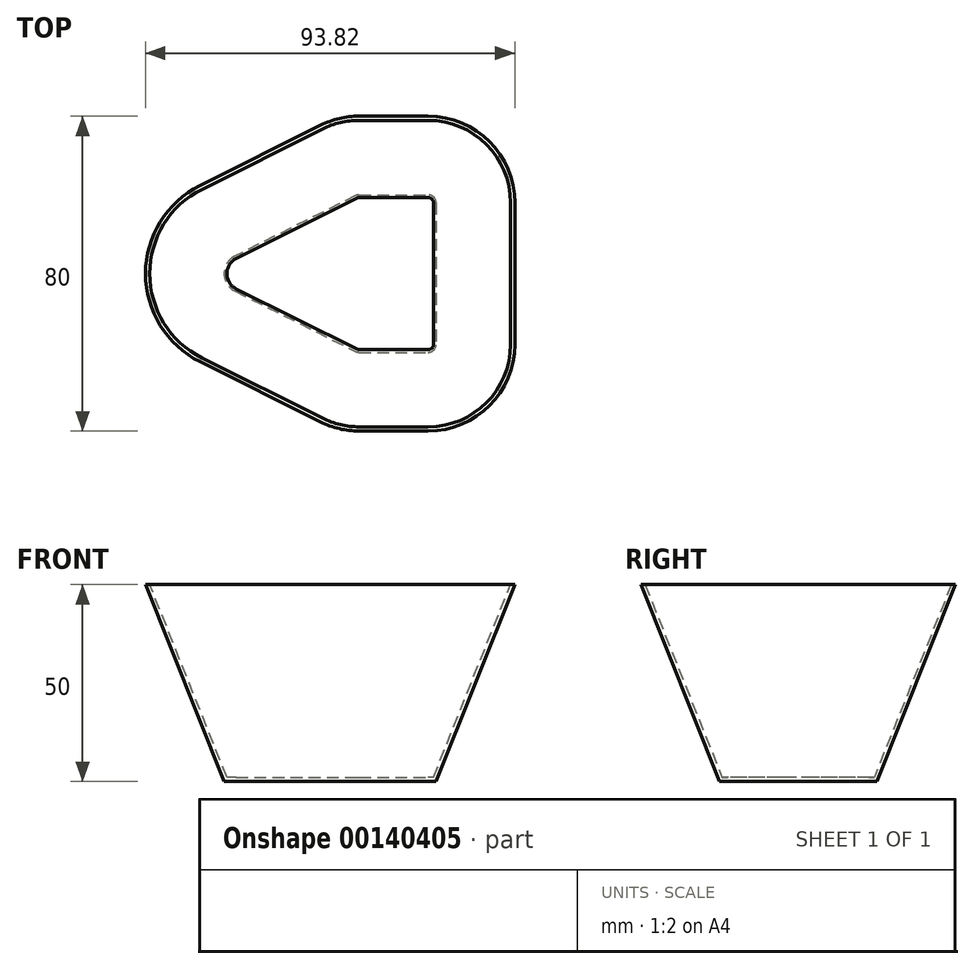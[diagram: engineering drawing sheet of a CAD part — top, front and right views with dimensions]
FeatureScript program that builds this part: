
annotation { "Feature Type Name" : "Feature", "Feature Type Description" : "" }
export const myFeature = defineFeature(function(context is Context, id is Id, definition is map)
    precondition{}
    {
        {
            var Q0;
            Q0=qCreatedBy(makeId("Top.planeOp"),FACE);
            var sketch = newSketch(context, id + "F0", { "sketchPlane" : qUnion([Q0])});
            skLineSegment(sketch, "E0.bottom", {"start": v(-25.46, 0.32) * mm, "end": v(-7.94, 0.32) * mm});
            skLineSegment(sketch, "E0.top", {"start": v(-25.46, -39.68) * mm, "end": v(-7.94, -39.68) * mm});
            skLineSegment(sketch, "E0.left", {"start": v(-25.94, 0.32) * mm, "end": v(-25.94, -39.68) * mm, "construction": true});
            skLineSegment(sketch, "E0.right", {"start": v(-5.94, -1.68) * mm, "end": v(-5.94, -37.68) * mm});
            skLineSegment(sketch, "E1", {"start": v(-26.36, 0.1) * mm, "end": v(-57, -15.2) * mm});
            skLineSegment(sketch, "E2", {"start": v(-57, -24.15) * mm, "end": v(-26.36, -39.47) * mm});
            skPoint(sketch, "E3.visualSharp", {"position": v(-65.94, -19.68) * mm});
            skArc(sketch, "E3.filletArc", {"start": v(-57, -15.2) * mm, "mid": v(-59.76, -19.68) * mm, "end": v(-57, -24.15) * mm});
            skPoint(sketch, "E4.visualSharp", {"position": v(-5.94, 0.32) * mm});
            skArc(sketch, "E4.filletArc", {"start": v(-5.94, -1.68) * mm, "mid": v(-6.52, -0.27) * mm, "end": v(-7.94, 0.32) * mm});
            skPoint(sketch, "E5.visualSharp", {"position": v(-5.94, -39.68) * mm});
            skArc(sketch, "E5.filletArc", {"start": v(-7.94, -39.68) * mm, "mid": v(-6.52, -39.1) * mm, "end": v(-5.94, -37.68) * mm});
            skPoint(sketch, "E6.visualSharp", {"position": v(-25.94, -39.68) * mm});
            skArc(sketch, "E6.filletArc", {"start": v(-26.36, -39.47) * mm, "mid": v(-25.92, -39.63) * mm, "end": v(-25.46, -39.68) * mm});
            skPoint(sketch, "E7.visualSharp", {"position": v(-25.94, 0.32) * mm});
            skArc(sketch, "E7.filletArc", {"start": v(-25.46, 0.32) * mm, "mid": v(-25.92, 0.27) * mm, "end": v(-26.36, 0.1) * mm});
            skSolve(sketch);
        }
        {
            var Q0;
            Q0=makeQuery(id+"F0.imprint","IMPRINT",FACE,{"disambiguationData":[TD([[makeQuery(id+"F0.imprint","IMPRINT",EDGE,{"derivedFrom":sQuery(id+"F0.wireOp",EDGE,"E0.bottom")}),-1.0]])]});
            cPlane(context, id + "F1", {"entities" : qUnion([Q0]), "cplaneType" : CPlaneType.OFFSET, "offset" : 50 * mm, "width" : 150 * mm, "height" : 150 * mm});
        }
        {
            var Q0;
            Q0=qCreatedBy(id+"F1.planeOp",FACE);
            var sketch = newSketch(context, id + "F2", { "sketchPlane" : qUnion([Q0])});
            skArc(sketch, "E8.0", {"start": v(-25.46, 20.32) * mm, "mid": v(-30.52, 19.73) * mm, "end": v(-35.3, 18) * mm});
            skLineSegment(sketch, "E8.1", {"start": v(-35.3, 18) * mm, "end": v(-65.94, 2.68) * mm});
            skLineSegment(sketch, "E8.2", {"start": v(-25.46, 20.32) * mm, "end": v(-7.94, 20.32) * mm});
            skArc(sketch, "E8.3", {"start": v(-65.94, 2.68) * mm, "mid": v(-79.76, -19.68) * mm, "end": v(-65.94, -42.04) * mm});
            skLineSegment(sketch, "E8.4", {"start": v(-65.94, -42.04) * mm, "end": v(-35.3, -57.36) * mm});
            skArc(sketch, "E8.5", {"start": v(-35.3, -57.36) * mm, "mid": v(-30.52, -59.1) * mm, "end": v(-25.46, -59.68) * mm});
            skArc(sketch, "E8.6", {"start": v(14.06, -1.68) * mm, "mid": v(7.62, 13.88) * mm, "end": v(-7.94, 20.32) * mm});
            skLineSegment(sketch, "E8.7", {"start": v(14.06, -1.68) * mm, "end": v(14.06, -37.68) * mm});
            skArc(sketch, "E8.8", {"start": v(-7.94, -59.68) * mm, "mid": v(7.62, -53.24) * mm, "end": v(14.06, -37.68) * mm});
            skLineSegment(sketch, "E8.9", {"start": v(-25.46, -59.68) * mm, "end": v(-7.94, -59.68) * mm});
            skSolve(sketch);
        }
        {
            var Q0;
            Q0=makeQuery(id+"F0.imprint","IMPRINT",FACE,{"disambiguationData":[TD([[makeQuery(id+"F0.imprint","IMPRINT",EDGE,{"derivedFrom":sQuery(id+"F0.wireOp",EDGE,"E0.bottom")}),-1.0]])]});
            var Q1;
            Q1=makeQuery(id+"F2.imprint","IMPRINT",FACE,{"disambiguationData":[TD([[makeQuery(id+"F2.imprint","IMPRINT",EDGE,{"derivedFrom":sQuery(id+"F2.wireOp",EDGE,"E8.0")}),1.0]])]});
            loft(context, id + "F3", {"sheetProfilesArray" : [{ "sheetProfileEntities" : qUnion([Q0]) }, { "sheetProfileEntities" : qUnion([Q1]) }]});
        }
        {
            var Q0;
            Q0=makeQuery(id+"F3.opLoft","CAP_FACE",FACE,{"disambiguationData":[OSD([makeQuery(id+"F2.imprint","IMPRINT",FACE,{"disambiguationData":[TD([[makeQuery(id+"F2.imprint","IMPRINT",EDGE,{"derivedFrom":sQuery(id+"F2.wireOp",EDGE,"E8.0")}),1.0]])]})])],"isStart":true});
            shell(context, id + "F4", {"entities" : qUnion([Q0]), "thickness" : 1 * mm});
        }
    });
